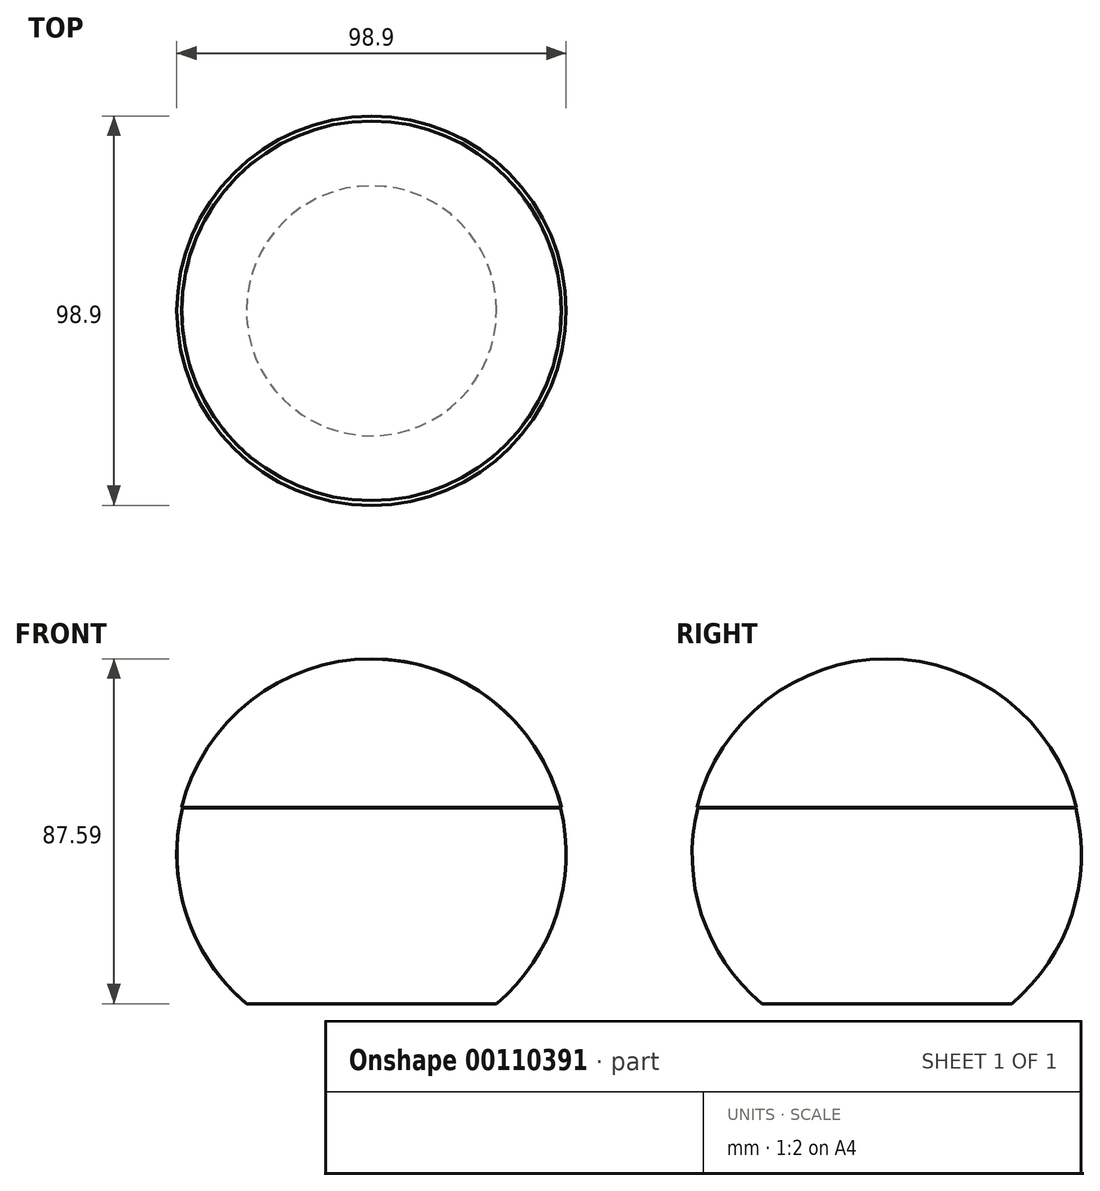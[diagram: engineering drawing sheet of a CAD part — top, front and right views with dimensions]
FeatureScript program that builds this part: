
annotation { "Feature Type Name" : "Feature", "Feature Type Description" : "" }
export const myFeature = defineFeature(function(context is Context, id is Id, definition is map)
    precondition{}
    {
        {
            var Q0;
            Q0=qCreatedBy(makeId("Front.planeOp"),FACE);
            var sketch = newSketch(context, id + "F0", { "sketchPlane" : qUnion([Q0])});
            skCircle(sketch, "E0", {"center": v(0, 0) * mm, "radius": 49.7 * mm});
            skLineSegment(sketch, "E1", {"start": v(-48.23, 11.95) * mm, "end": v(48.23, 11.95) * mm});
            skLineSegment(sketch, "E2", {"start": v(0, 49.7) * mm, "end": v(0, 11.95) * mm});
            skLineSegment(sketch, "E3", {"start": v(0, 11.95) * mm, "end": v(0, -49.7) * mm});
            skSolve(sketch);
        }
        {
            var Q0;
            {var subQ3=sQuery(id+"F0.wireOp",EDGE,"E2");Q0=makeQuery(id+"F0.imprint","IMPRINT",FACE,{"disambiguationData":[TD([[makeQuery(id+"F0.imprint","IMPRINT",EDGE,{"derivedFrom":subQ3}),-1.0]])]});}
            var Q1;
            Q1=sQuery(id+"F0.wireOp",EDGE,"E2");
            revolve(context, id + "F1", {"entities" : qUnion([Q0]), "axis" : qUnion([Q1]), "revolveType" : RevolveType.FULL});
        }
        {
            var Q0;
            Q0=qCreatedBy(makeId("Front.planeOp"),FACE);
            var sketch = newSketch(context, id + "F2", { "sketchPlane" : qUnion([Q0])});
            skCircle(sketch, "E4", {"center": v(0, 0) * mm, "radius": 49.45 * mm});
            skLineSegment(sketch, "E5", {"start": v(0, 11.85) * mm, "end": v(0, -49.45) * mm});
            skLineSegment(sketch, "E6", {"start": v(0, 11.85) * mm, "end": v(-48, 11.85) * mm});
            skLineSegment(sketch, "E7", {"start": v(0, 11.85) * mm, "end": v(48, 11.85) * mm});
            skSolve(sketch);
        }
        {
            var Q0;
            {var subQ0=sQuery(id+"F2.wireOp",EDGE,"E5");Q0=makeQuery(id+"F2.imprint","IMPRINT",FACE,{"disambiguationData":[TD([[makeQuery(id+"F2.imprint","IMPRINT",EDGE,{"derivedFrom":subQ0}),-1.0]])]});}
            var Q1;
            Q1=sQuery(id+"F2.wireOp",EDGE,"E5");
            revolve(context, id + "F3", {"entities" : qUnion([Q0]), "axis" : qUnion([Q1]), "revolveType" : RevolveType.FULL});
        }
        {
            var Q0;
            Q0=qCreatedBy(makeId("Front.planeOp"),FACE);
            var sketch = newSketch(context, id + "F4", { "sketchPlane" : qUnion([Q0])});
            skLineSegment(sketch, "E8", {"start": v(-33.88, -37.9) * mm, "end": v(34.86, -37.9) * mm});
            skLineSegment(sketch, "E9", {"start": v(34.86, -37.9) * mm, "end": v(34.86, -54.94) * mm});
            skLineSegment(sketch, "E10", {"start": v(34.86, -54.94) * mm, "end": v(-33.88, -54.94) * mm});
            skLineSegment(sketch, "E11", {"start": v(-33.88, -54.94) * mm, "end": v(-33.88, -37.9) * mm});
            skSolve(sketch);
        }
        {
            var Q0;
            Q0 = qSketchRegion(id + "F4", true);
            extrude(context, id + "F5", {"entities" : qUnion([Q0]), "operationType" : NewBodyOperationType.REMOVE, "oppositeDirection" : true, "depth" : 52.54 * mm, "hasSecondDirection" : true, "secondDirectionOppositeDirection" : false, "secondDirectionDepth" : 51.57 * mm});
        }
    });
